# Revit family: rba-bim-rbam-40-tmvb
name_source: partatom
category: Plumbing Fixtures
revit_build: Autodesk Revit 2018 (Build: 20170223_1515(x64)
units: mm (PartAtom-declared; Revit-internal decimal feet)

## family parameters
Always vertical = Yes
Cut with Voids When Loaded = No
OmniClass Number = 23.45.00.00
OmniClass Title = Sanitary, Laundry, and Cleaning Equipment
Part Type = Normal
Room Calculation Point = No
Round Connector Dimension = Use Diameter
Shared = No
Work Plane-Based = No

## types (1)
- RBAM-40-TMVB_475w x 475h x 80-102d
    Conduit = Plastic, Opaque White
    Depth = 80-102 Adjustable
    Description = Pre-Plumbed Water Heater & TMV
    Electrical Connector = Hard Wired
    Fitting = DZR Brass
    Full Load Current = 40 Amps
    Height = 475 mm
    In-Wall Box = Stainless Steel - Type 304 - Satin Finish
    Manufacturer = RBA Group
    Materials and Finishes = Stainless Steel - Type 304 - Satin Finish
    Model = RBAM-40-TMVB
    Modified Issue = 20200506.01
    Phases = Single Phase
    Piping = Copper
    Radius = 13 mm
    Total Watts = 9600 W
    Type Comments = Refer website TD Sheet for technical details, modelled without door
    URL = www.rba.com.au
    Voltage = 240 V
    Width = 475 mm

## geometry (parser evidence)
native form markers: Blend x20, Sweep x18
no freeform markers — native parametric forms only
